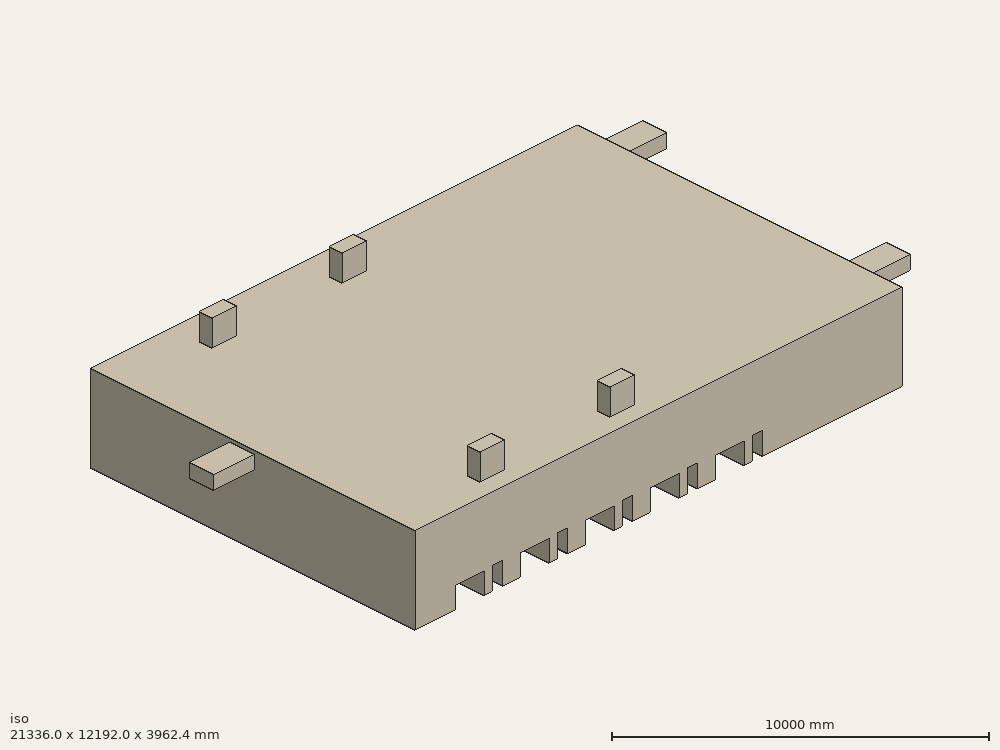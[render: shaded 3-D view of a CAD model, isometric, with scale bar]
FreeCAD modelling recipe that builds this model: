
FCSTD DOCUMENT  (FreeCAD 0.18R14555 (Git shallow))
Label: flow_domain
License: All rights reserved
LicenseURL: http://en.wikipedia.org/wiki/All_rights_reserved
objects: Part::Box×19, Part::MultiFuse×12, Part::Mirroring×1, Part::Cut×1
note: 33 computed .brp shape members not serialized (recipe doc carries the construction recipe); baked Part::Feature solids carry a one-line shape summary decoded from their .brp

FEATURE [Part::Box] Box001  label="Bed 1"
  AttacherType = Attacher::AttachEngine3D
  Height = 762
  Length = 1066.8
  Width = 1981.2
FEATURE [Part::Box] Box002  label="Table 1"
  AttacherType = Attacher::AttachEngine3D
  Height = 798.576
  Length = 396.24
  Placement = pos=(1371.6,0,0) rot=(0,0,1;0rad)
  Width = 396.24
FEATURE [Part::MultiFuse] Fusion  label="Set 1"
  Shapes = -> [Box002,Box001]
FEATURE [Part::Box] Box003  label="Bed 002"
  AttacherType = Attacher::AttachEngine3D
  Height = 762
  Length = 1066.8
  Width = 1981.2
FEATURE [Part::Box] Box004  label="Table 002"
  AttacherType = Attacher::AttachEngine3D
  Height = 798.576
  Length = 396.24
  Placement = pos=(1371.6,0,0) rot=(0,0,1;0rad)
  Width = 396.24
FEATURE [Part::MultiFuse] Fusion001  label="Set 2"
  Placement = pos=(2438.4,0,0) rot=(0,0,1;0rad)
  Shapes = -> [Box004,Box003]
FEATURE [Part::Box] Box005  label="Table 003"
  AttacherType = Attacher::AttachEngine3D
  Height = 798.576
  Length = 396.24
  Placement = pos=(1371.6,0,0) rot=(0,0,1;0rad)
  Width = 396.24
FEATURE [Part::Box] Box006  label="Bed 003"
  AttacherType = Attacher::AttachEngine3D
  Height = 762
  Length = 1066.8
  Width = 1981.2
FEATURE [Part::MultiFuse] Fusion002  label="Set 3"
  Placement = pos=(4876.8,0,0) rot=(0,0,1;0rad)
  Shapes = -> [Box005,Box006]
FEATURE [Part::Box] Box007  label="Bed 004"
  AttacherType = Attacher::AttachEngine3D
  Height = 762
  Length = 1066.8
  Width = 1981.2
FEATURE [Part::Box] Box008  label="Table 004"
  AttacherType = Attacher::AttachEngine3D
  Height = 798.576
  Length = 396.24
  Placement = pos=(1371.6,0,0) rot=(0,0,1;0rad)
  Width = 396.24
FEATURE [Part::MultiFuse] Fusion003  label="Set 4"
  Placement = pos=(7315.2,0,0) rot=(0,0,1;0rad)
  Shapes = -> [Box008,Box007]
FEATURE [Part::Box] Box009  label="Table 005"
  AttacherType = Attacher::AttachEngine3D
  Height = 798.576
  Length = 396.24
  Placement = pos=(1371.6,0,0) rot=(0,0,1;0rad)
  Width = 396.24
FEATURE [Part::Box] Box010  label="Bed 005"
  AttacherType = Attacher::AttachEngine3D
  Height = 762
  Length = 1066.8
  Width = 1981.2
FEATURE [Part::MultiFuse] Fusion004  label="Set 5"
  Placement = pos=(9753.6,0,0) rot=(0,0,1;0rad)
  Shapes = -> [Box009,Box010]
FEATURE [Part::MultiFuse] Fusion005  label="right beds"
  Shapes = -> [Fusion001,Fusion002,Fusion003,Fusion004,Fusion]
FEATURE [Part::Mirroring] Part__Mirroring  label="left beds"
  Base = (0,6096,0)
  Normal = (0,1,0)
  Source = -> Fusion005
FEATURE [Part::Box] Box011  label="Nurse Station"
  AttacherType = Attacher::AttachEngine3D
  Height = 1219.2
  Length = 3048
  Placement = pos=(15240,7620,0) rot=(0,0,1;0rad)
  Width = 4572
FEATURE [Part::Box] Box012  label="main inlet"
  AttacherType = Attacher::AttachEngine3D
  Height = 487.68
  Length = 2438.4
  Placement = pos=(17373.6,1219.2,2438.4) rot=(0,0,1;0rad)
  Width = 914.4
FEATURE [Part::Box] Box013  label="main outlet"
  AttacherType = Attacher::AttachEngine3D
  Height = 487.68
  Length = 2438.4
  Placement = pos=(-1524,6040.43,2438.4) rot=(0,0,1;0rad)
  Width = 914.4
FEATURE [Part::Box] Box016  label="branch002"
  AttacherType = Attacher::AttachEngine3D
  Height = 1219.2
  Length = 914.4
  Placement = pos=(7924.8,609.6,2743.2) rot=(0,0,1;0rad)
  Width = 487.68
FEATURE [Part::Box] Box017  label="branch003"
  AttacherType = Attacher::AttachEngine3D
  Height = 1219.2
  Length = 914.4
  Placement = pos=(7924.8,10668,2743.2) rot=(0,0,1;0rad)
  Width = 487.68
FEATURE [Part::Box] Box018  label="branch004"
  AttacherType = Attacher::AttachEngine3D
  Height = 1219.2
  Length = 914.4
  Placement = pos=(3048,609.6,2743.2) rot=(0,0,1;0rad)
  Width = 487.68
FEATURE [Part::Box] Box019  label="branch005"
  AttacherType = Attacher::AttachEngine3D
  Height = 1219.2
  Length = 914.4
  Placement = pos=(3048,10668,2743.2) rot=(0,0,1;0rad)
  Width = 487.68
FEATURE [Part::MultiFuse] Fusion006  label="all beds"
  Placement = pos=(1524,0,0) rot=(0,0,1;0rad)
  Shapes = -> [Part__Mirroring,Fusion005]
FEATURE [Part::Box] Box  label="Room"
  AttacherType = Attacher::AttachEngine3D
  Height = 3048
  Length = 18288
  Width = 12192
FEATURE [Part::MultiFuse] Fusion010  label="surfaces"
  Shapes = -> [Fusion006,Box011]
FEATURE [Part::MultiFuse] Fusion011  label="branch_ducts"
  Shapes = -> [Box016,Box017,Box018,Box019]
FEATURE [Part::Box] Box020  label="main inlet001"
  AttacherType = Attacher::AttachEngine3D
  Height = 487.68
  Length = 2438.4
  Placement = pos=(17373.6,10363.2,2438.4) rot=(0,0,1;0rad)
  Width = 914.4
FEATURE [Part::MultiFuse] Fusion012  label="main_ducts"
  Shapes = -> [Box020,Box012,Box013]
FEATURE [Part::MultiFuse] Fusion013
  Shapes = -> [Fusion012,Fusion011]
FEATURE [Part::MultiFuse] Fusion014
  Shapes = -> [Box,Fusion013]
FEATURE [Part::Cut] Cut
  Base = -> Fusion014
  Tool = -> Fusion010
